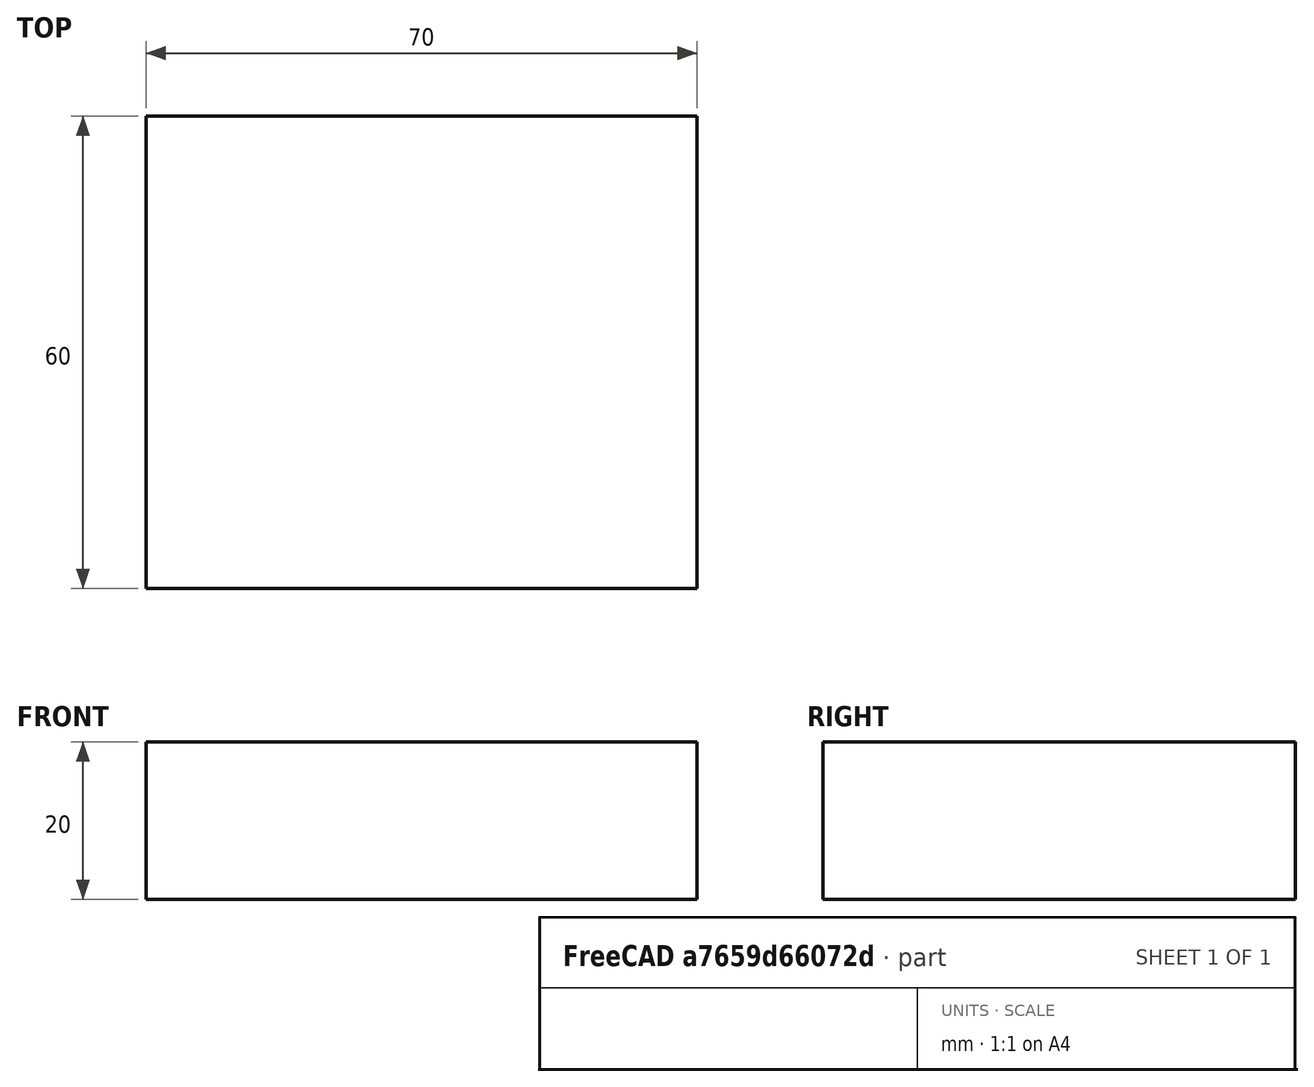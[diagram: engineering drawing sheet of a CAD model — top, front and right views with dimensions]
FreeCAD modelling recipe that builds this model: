
FCSTD DOCUMENT  (FreeCAD 0.21R33694 (Git))
Label: OJT1_T018_P01_rectangle_fixat
License: All rights reserved
LicenseURL: http://en.wikipedia.org/wiki/All_rights_reserved
objects: Sketcher::SketchObject×1, PartDesign::Pad×1, PartDesign::Body×1
note: 4 computed .brp shape members not serialized (recipe doc carries the construction recipe); baked Part::Feature solids carry a one-line shape summary decoded from their .brp

FEATURE [Sketcher::SketchObject] Sketch
  FullyConstrained = false
  MapMode = 5
  Support = -> [XY_Plane]
  sketch-geometry (8):
    g0: LineSegment StartX=-29.6837 StartY=40.0664 StartZ=0 EndX=40.3163 EndY=40.0664 EndZ=0
    g1: LineSegment StartX=-29.6837 StartY=40.0664 StartZ=0 EndX=-29.6837 EndY=-19.9336 EndZ=0
    g2: LineSegment StartX=-29.6837 StartY=-19.9336 StartZ=0 EndX=40.3163 EndY=-19.9336 EndZ=0
    g3: LineSegment StartX=40.3163 StartY=40.0664 StartZ=0 EndX=40.3163 EndY=-19.9336 EndZ=0
    g4: GeomPoint X=40.3163 Y=40.0664 Z=0
    g5: GeomPoint X=40.3163 Y=40.0664 Z=0
    g6: GeomPoint X=40.3163 Y=40.0664 Z=0
    g7: GeomPoint X=40.3163 Y=40.0664 Z=0
  constraints (14):
    c: Coincident(g4,g0)
    c: Coincident(g5,g3)
    c: Coincident(g6,g0)
    c: Coincident(g7,g3)
    c: Coincident(g0,g3)
    c: Coincident(g0,g1)
    c: Coincident(g2,g3)
    c: Coincident(g1,g2)
    c: Horizontal(g0)
    c: Horizontal(g2)
    c: Vertical(g1)
    c: Vertical(g3)
    c: DistanceY(g1,g1) = 60
    c: DistanceX(g0,g0) = 70
FEATURE [PartDesign::Pad] Pad
  Direction = (0,0,1)
  Length = 20
  Length2 = 10
  Profile = -> Sketch
  ReferenceAxis = -> Sketch [N_Axis]
  Type = 0
FEATURE [PartDesign::Body] Body
  Group = -> [Sketch,Pad]
  Origin = -> Origin
  Tip = -> Pad
